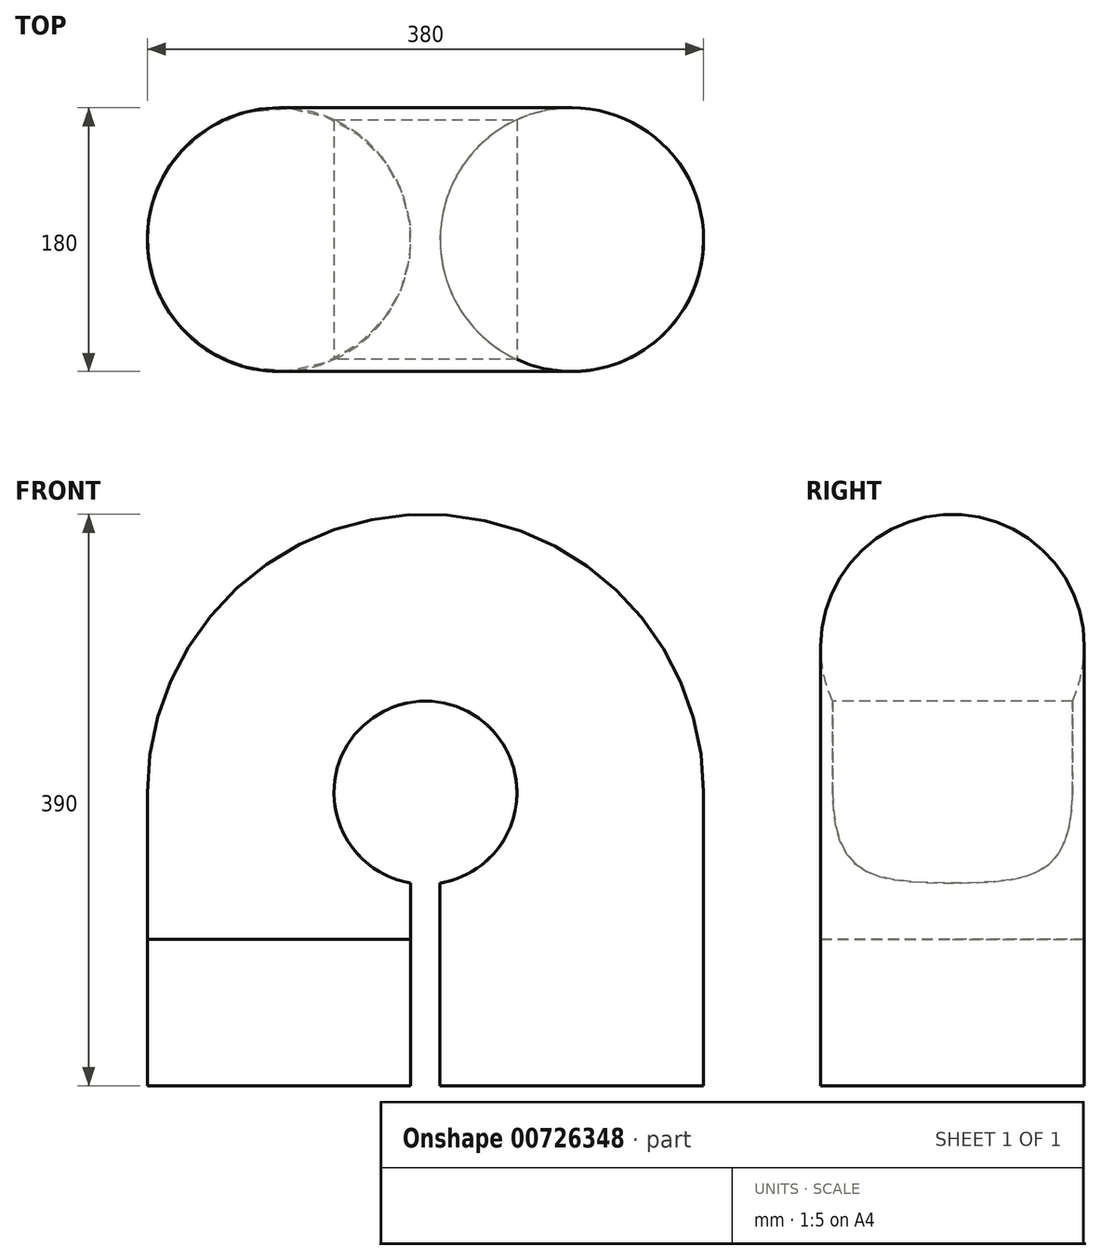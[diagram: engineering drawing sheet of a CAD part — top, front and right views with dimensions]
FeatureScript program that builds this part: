
annotation { "Feature Type Name" : "Feature", "Feature Type Description" : "" }
export const myFeature = defineFeature(function(context is Context, id is Id, definition is map)
    precondition{}
    {
        {
            var Q0;
            Q0=qCreatedBy(makeId("Front.planeOp"),FACE);
            var sketch = newSketch(context, id + "F0", { "sketchPlane" : qUnion([Q0])});
            skLineSegment(sketch, "E0.left", {"start": v(100, -0.86) * mm, "end": v(100, 100) * mm});
            skLineSegment(sketch, "E0.right", {"start": v(-100, 0) * mm, "end": v(-100, 100) * mm});
            skLineSegment(sketch, "E1", {"start": v(-100, 0) * mm, "end": v(-100, -100) * mm});
            skLineSegment(sketch, "E2", {"start": v(100, -0.86) * mm, "end": v(100, -100) * mm});
            skArc(sketch, "E3", {"start": v(-100, 100) * mm, "mid": v(0, 200) * mm, "end": v(100, 100) * mm});
            skSolve(sketch);
        }
        {
            var Q0;
            Q0=qCreatedBy(makeId("Top.planeOp"),FACE);
            var sketch = newSketch(context, id + "F1", { "sketchPlane" : qUnion([Q0])});
            skCircle(sketch, "E4", {"center": v(100, 0) * mm, "radius": 90 * mm});
            skSolve(sketch);
        }
        {
            var Q0;
            Q0=makeQuery(id+"F1.imprint","IMPRINT",FACE,{"disambiguationData":[TD([[makeQuery(id+"F1.imprint","IMPRINT",EDGE,{"derivedFrom":sQuery(id+"F1.wireOp",EDGE,"E4")}),1.0]])]});
            var Q1;
            Q1=sQuery(id+"F0.wireOp",EDGE,"E2");
            var Q2;
            Q2=sQuery(id+"F0.wireOp",EDGE,"E0.left");
            var Q3;
            Q3=sQuery(id+"F0.wireOp",EDGE,"E3");
            var Q4;
            Q4=sQuery(id+"F0.wireOp",EDGE,"E0.right");
            var Q5;
            Q5=sQuery(id+"F0.wireOp",EDGE,"E1");
            sweep(context, id + "F2", {"profiles" : qUnion([Q0]), "path" : qUnion([Q1, Q2, Q3, Q4, Q5])});
        }
        {
            var Q0;
            Q0=qCreatedBy(makeId("Front.planeOp"),FACE);
            var sketch = newSketch(context, id + "F3", { "sketchPlane" : qUnion([Q0])});
            skCircle(sketch, "E5", {"center": v(0, 100) * mm, "radius": 62.5 * mm});
            skSolve(sketch);
        }
        {
            var Q0;
            Q0=qSketchRegion(id+"F3",true);
            extrude(context, id + "F4", {"entities" : qUnion([Q0]), "operationType" : NewBodyOperationType.REMOVE, "endBound" : BoundingType.SYMMETRIC, "oppositeDirection" : true, "depth" : 200 * mm, "offsetDistance" : 25 * mm});
        }
    });
